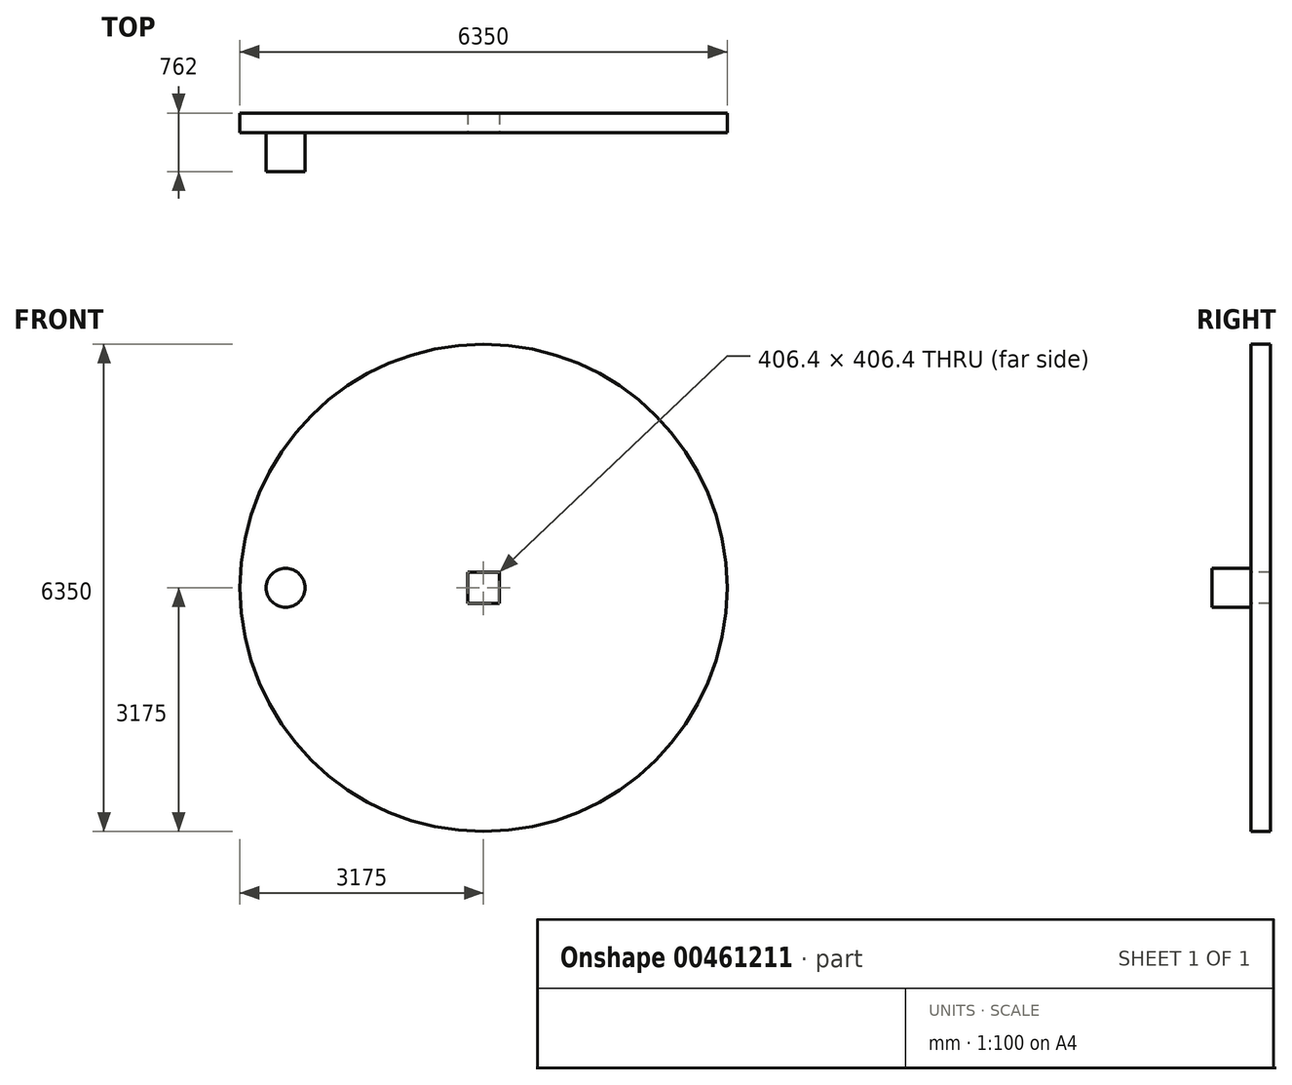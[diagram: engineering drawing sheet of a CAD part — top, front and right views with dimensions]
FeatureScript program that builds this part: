
annotation { "Feature Type Name" : "Feature", "Feature Type Description" : "" }
export const myFeature = defineFeature(function(context is Context, id is Id, definition is map)
    precondition{}
    {
        {
            var Q0;
            Q0=qCreatedBy(makeId("Front.planeOp"),FACE);
            var sketch = newSketch(context, id + "F0", { "sketchPlane" : qUnion([Q0])});
            skCircle(sketch, "E0", {"center": v(0, 0) * mm, "radius": 3175 * mm});
            skSolve(sketch);
        }
        {
            var Q0;
            Q0 = qSketchRegion(id + "F0", true);
            extrude(context, id + "F1", {"entities" : qUnion([Q0]), "depth" : 254 * mm});
        }
        {
            var Q0;
            Q0=makeQuery(id+"F1.opExtrude","CAP_FACE",FACE,{"disambiguationData":[OSD([sQuery(id+"F0.wireOp",EDGE,"E0")])],"isStart":false});
            var sketch = newSketch(context, id + "F2", { "sketchPlane" : qUnion([Q0])});
            skCircle(sketch, "E1", {"center": v(-2580.09, 0) * mm, "radius": 254 * mm});
            skSolve(sketch);
        }
        {
            var Q0;
            Q0=makeQuery(id+"F2.imprint","IMPRINT",FACE,{"disambiguationData":[TD([[makeQuery(id+"F2.imprint","IMPRINT",EDGE,{"derivedFrom":sQuery(id+"F2.wireOp",EDGE,"E1")}),1.0]])]});
            extrude(context, id + "F3", {"entities" : qUnion([Q0]), "operationType" : NewBodyOperationType.ADD, "depth" : 508 * mm});
        }
        {
            var Q0;
            Q0=makeQuery(id+"F1.opExtrude","CAP_FACE",FACE,{"disambiguationData":[OSD([sQuery(id+"F0.wireOp",EDGE,"E0")])],"isStart":false});
            var sketch = newSketch(context, id + "F4", { "sketchPlane" : qUnion([Q0])});
            skLineSegment(sketch, "E2", {"start": v(0, 203.2) * mm, "end": v(203.2, 203.2) * mm});
            skLineSegment(sketch, "E3", {"start": v(203.2, 203.2) * mm, "end": v(203.2, -203.2) * mm});
            skLineSegment(sketch, "E4", {"start": v(203.2, -203.2) * mm, "end": v(-203.2, -203.2) * mm});
            skLineSegment(sketch, "E5", {"start": v(-203.2, -203.2) * mm, "end": v(-203.2, 203.2) * mm});
            skLineSegment(sketch, "E6", {"start": v(-203.2, 203.2) * mm, "end": v(0, 203.2) * mm});
            skSolve(sketch);
        }
        {
            var Q0;
            Q0 = qSketchRegion(id + "F4", true);
            extrude(context, id + "F5", {"entities" : qUnion([Q0]), "operationType" : NewBodyOperationType.REMOVE, "oppositeDirection" : true, "depth" : 254 * mm});
        }
    });
